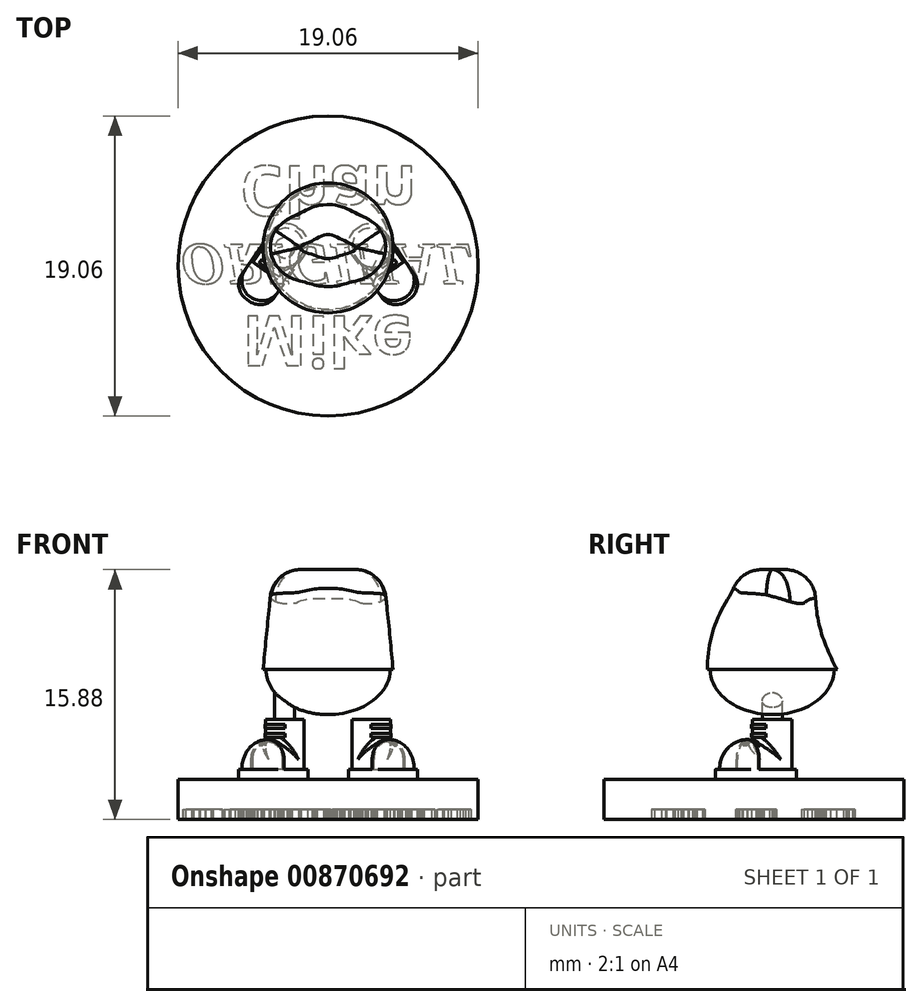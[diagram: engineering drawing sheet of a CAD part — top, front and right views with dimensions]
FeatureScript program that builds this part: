
annotation { "Feature Type Name" : "Feature", "Feature Type Description" : "" }
export const myFeature = defineFeature(function(context is Context, id is Id, definition is map)
    precondition{}
    {
        {
            var Q0;
            Q0=qCreatedBy(makeId("Top.planeOp"),FACE);
            var sketch = newSketch(context, id + "F0", { "sketchPlane" : qUnion([Q0])});
            skCircle(sketch, "E0", {"center": v(0, 0) * mm, "radius": 9.53 * mm});
            skSolve(sketch);
        }
        {
            var Q0;
            Q0=qSketchRegion(id+"F0",true);
            extrude(context, id + "F1", {"entities" : qUnion([Q0]), "depth" : 2.54 * mm, "offsetDistance" : 25.4 * mm});
        }
        {
            var Q0;
            Q0=qCreatedBy(makeId("Front.planeOp"),FACE);
            cPlane(context, id + "F2", {"entities" : qUnion([Q0]), "cplaneType" : CPlaneType.OFFSET, "offset" : 5.08 * mm, "oppositeDirection" : true, "width" : 152.4 * mm, "height" : 152.4 * mm});
        }
        {
            var Q0;
            Q0=qCreatedBy(id+"F2.planeOp",FACE);
            var sketch = newSketch(context, id + "F3", { "sketchPlane" : qUnion([Q0])});
            skLineSegment(sketch, "E1", {"start": v(0, 0) * mm, "end": v(0, 37.35) * mm, "construction": true});
            skSolve(sketch);
        }
        {
            var Q0;
            Q0=sQuery(id+"F3.wireOp",EDGE,"E1");
            var Q1;
            Q1=qCreatedBy(id+"F2.planeOp",FACE);
            cPlane(context, id + "F4", {"entities" : qUnion([Q0, Q1]), "cplaneType" : CPlaneType.LINE_ANGLE, "offset" : 25.4 * mm, "angle" : 55 * degree, "width" : 152.4 * mm, "height" : 152.4 * mm});
        }
        {
            var Q0;
            Q0=qCreatedBy(id+"F4.planeOp",FACE);
            var sketch = newSketch(context, id + "F5", { "sketchPlane" : qUnion([Q0])});
            skLineSegment(sketch, "E2", {"start": v(0, 0) * mm, "end": v(0, 19.24) * mm, "construction": true});
            skLineSegment(sketch, "E3", {"start": v(-0.89, 3.18) * mm, "end": v(4.45, 3.18) * mm});
            skArc(sketch, "E4", {"start": v(4.45, 3.18) * mm, "mid": v(3.89, 4.52) * mm, "end": v(2.54, 5.08) * mm});
            skLineSegment(sketch, "E5", {"start": v(2.54, 3.18) * mm, "end": v(2.54, 5.08) * mm});
            skLineSegment(sketch, "E6", {"start": v(2.54, 4.95) * mm, "end": v(1.9, 4.95) * mm});
            skLineSegment(sketch, "E7", {"start": v(-0.89, 3.18) * mm, "end": v(-0.89, 2.54) * mm});
            skLineSegment(sketch, "E8", {"start": v(-0.89, 2.54) * mm, "end": v(4.7, 2.54) * mm});
            skLineSegment(sketch, "E9", {"start": v(4.7, 2.54) * mm, "end": v(4.7, 3.18) * mm});
            skLineSegment(sketch, "E10", {"start": v(4.7, 3.18) * mm, "end": v(4.45, 3.18) * mm});
            skLineSegment(sketch, "E11", {"start": v(-0.64, 3.18) * mm, "end": v(-0.64, 6.35) * mm});
            skLineSegment(sketch, "E12", {"start": v(-0.64, 6.35) * mm, "end": v(1.9, 6.35) * mm});
            skLineSegment(sketch, "E13", {"start": v(1.9, 6.35) * mm, "end": v(1.9, 4.95) * mm});
            skSolve(sketch);
        }
        {
            var Q0;
            Q0=qSketchRegion(id+"F5",true);
            extrude(context, id + "F6", {"entities" : qUnion([Q0]), "endBound" : BoundingType.SYMMETRIC, "depth" : 2.54 * mm, "offsetDistance" : 25.4 * mm});
        }
        {
            var Q0;
            Q0=makeQuery(id+"F6.opExtrude","SWEPT_FACE",FACE,{"disambiguationData":[OSD([sQuery(id+"F5.wireOp",EDGE,"E5")])]});
            var sketch = newSketch(context, id + "F7", { "sketchPlane" : qUnion([Q0])});
            skLineSegment(sketch, "E14", {"start": v(4.31, 3.18) * mm, "end": v(4.06, 3.18) * mm});
            skLineSegment(sketch, "E15", {"start": v(4.06, 3.18) * mm, "end": v(4.06, 6.99) * mm});
            skLineSegment(sketch, "E16", {"start": v(4.06, 6.99) * mm, "end": v(4.31, 6.99) * mm});
            skLineSegment(sketch, "E17", {"start": v(4.31, 6.99) * mm, "end": v(4.31, 3.18) * mm});
            skLineSegment(sketch, "E18.MirrorCS", {"start": v(1.52, 6.99) * mm, "end": v(1.52, 3.18) * mm});
            skLineSegment(sketch, "E19.MirrorCS", {"start": v(1.77, 6.99) * mm, "end": v(1.52, 6.99) * mm});
            skLineSegment(sketch, "E20.MirrorCS", {"start": v(1.77, 3.18) * mm, "end": v(1.77, 6.99) * mm});
            skPoint(sketch, "E21.orphan", {"position": v(1.23, 3.18) * mm});
            skLineSegment(sketch, "E22.trimOffspring", {"start": v(1.77, 3.18) * mm, "end": v(1.52, 3.18) * mm});
            skSolve(sketch);
        }
        {
            var Q0;
            Q0=qSketchRegion(id+"F7",true);
            extrude(context, id + "F8", {"entities" : qUnion([Q0]), "operationType" : NewBodyOperationType.REMOVE, "endBound" : BoundingType.THROUGH_ALL, "depth" : 25.4 * mm, "offsetDistance" : 25.4 * mm});
        }
        {
            var Q0;
            Q0=makeQuery(id+"F8.boolean.opBoolean","INTERSECT",EDGE,{"derivedFrom":[makeQuery(id+"F6.opExtrude","SWEPT_FACE",FACE,{"disambiguationData":[OSD([sQuery(id+"F5.wireOp",EDGE,"E6")])]}),makeQuery(id+"F8.opExtrude","SWEPT_FACE",FACE,{"disambiguationData":[OSD([sQuery(id+"F7.wireOp",EDGE,"E15")])]})]});
            var Q1;
            Q1=makeQuery(id+"F8.boolean.opBoolean","INTERSECT",EDGE,{"derivedFrom":[makeQuery(id+"F6.opExtrude","SWEPT_FACE",FACE,{"disambiguationData":[OSD([sQuery(id+"F5.wireOp",EDGE,"E6")])]}),makeQuery(id+"F8.opExtrude","SWEPT_FACE",FACE,{"disambiguationData":[OSD([sQuery(id+"F7.wireOp",EDGE,"E20.MirrorCS")])]})]});
            var Q2;
            Q2=makeQuery(id+"F8.boolean.opBoolean","INTERSECT",EDGE,{"derivedFrom":[makeQuery(id+"F6.opExtrude","SWEPT_FACE",FACE,{"disambiguationData":[OSD([sQuery(id+"F5.wireOp",EDGE,"E13")])]}),makeQuery(id+"F8.opExtrude","SWEPT_FACE",FACE,{"disambiguationData":[OSD([sQuery(id+"F7.wireOp",EDGE,"E15")])]})]});
            var Q3;
            Q3=makeQuery(id+"F8.boolean.opBoolean","INTERSECT",EDGE,{"derivedFrom":[makeQuery(id+"F6.opExtrude","SWEPT_FACE",FACE,{"disambiguationData":[OSD([sQuery(id+"F5.wireOp",EDGE,"E13")])]}),makeQuery(id+"F8.opExtrude","SWEPT_FACE",FACE,{"disambiguationData":[OSD([sQuery(id+"F7.wireOp",EDGE,"E20.MirrorCS")])]})]});
            var Q4;
            Q4=makeQuery(id+"F8.boolean.opBoolean","INTERSECT",EDGE,{"derivedFrom":[makeQuery(id+"F6.opExtrude","SWEPT_FACE",FACE,{"disambiguationData":[OSD([sQuery(id+"F5.wireOp",EDGE,"E11")])]}),makeQuery(id+"F8.opExtrude","SWEPT_FACE",FACE,{"disambiguationData":[OSD([sQuery(id+"F7.wireOp",EDGE,"E20.MirrorCS")])]})]});
            var Q5;
            Q5=makeQuery(id+"F8.boolean.opBoolean","INTERSECT",EDGE,{"derivedFrom":[makeQuery(id+"F6.opExtrude","SWEPT_FACE",FACE,{"disambiguationData":[OSD([sQuery(id+"F5.wireOp",EDGE,"E11")])]}),makeQuery(id+"F8.opExtrude","SWEPT_FACE",FACE,{"disambiguationData":[OSD([sQuery(id+"F7.wireOp",EDGE,"E15")])]})]});
            fillet(context, id + "F9", {"entities" : qUnion([Q0, Q1, Q2, Q3, Q4, Q5]), "radius" : 1.14 * mm, "tangentPropagation" : true, "allowEdgeOverflow" : false});
        }
        {
            var Q0;
            Q0=makeQuery(id+"F6.opExtrude","CAP_EDGE",EDGE,{"disambiguationData":[OSD([sQuery(id+"F5.wireOp",EDGE,"E4")])],"isStart":false});
            var Q1;
            Q1=makeQuery(id+"F6.opExtrude","CAP_EDGE",EDGE,{"disambiguationData":[OSD([sQuery(id+"F5.wireOp",EDGE,"E4")])],"isStart":true});
            fillet(context, id + "F10", {"entities" : qUnion([Q0, Q1]), "radius" : 1.27 * mm, "tangentPropagation" : true, "allowEdgeOverflow" : false});
        }
        {
            var Q0;
            Q0=makeQuery(id+"F6.opExtrude","CAP_EDGE",EDGE,{"disambiguationData":[OSD([sQuery(id+"F5.wireOp",EDGE,"E9")])],"isStart":false});
            var Q1;
            Q1=makeQuery(id+"F6.opExtrude","CAP_EDGE",EDGE,{"disambiguationData":[OSD([sQuery(id+"F5.wireOp",EDGE,"E7")])],"isStart":false});
            var Q2;
            Q2=makeQuery(id+"F6.opExtrude","CAP_EDGE",EDGE,{"disambiguationData":[OSD([sQuery(id+"F5.wireOp",EDGE,"E7")])],"isStart":true});
            var Q3;
            Q3=makeQuery(id+"F6.opExtrude","CAP_EDGE",EDGE,{"disambiguationData":[OSD([sQuery(id+"F5.wireOp",EDGE,"E9")])],"isStart":true});
            fillet(context, id + "F11", {"entities" : qUnion([Q0, Q1, Q2, Q3]), "radius" : 1.14 * mm, "tangentPropagation" : true, "allowEdgeOverflow" : false});
        }
        {
            var Q0;
            {var subQ0=makeQuery(id+"F8.opExtrude","SWEPT_FACE",FACE,{"disambiguationData":[OSD([sQuery(id+"F7.wireOp",EDGE,"E15")])]});Q0=makeQuery(id+"F9.opFillet","BLEND_EDGE",EDGE,{"blendedFrom":[makeQuery(id+"F8.boolean.opBoolean","INTERSECT",EDGE,{"derivedFrom":[makeQuery(id+"F6.opExtrude","SWEPT_FACE",FACE,{"disambiguationData":[OSD([sQuery(id+"F5.wireOp",EDGE,"E6")])]}),subQ0]}),makeQuery(id+"F8.boolean.opBoolean","INTERSECT",EDGE,{"derivedFrom":[makeQuery(id+"F6.opExtrude","SWEPT_FACE",FACE,{"disambiguationData":[OSD([sQuery(id+"F5.wireOp",EDGE,"E13")])]}),subQ0]})],"blendedInto":[]});}
            fillet(context, id + "F12", {"entities" : qUnion([Q0]), "radius" : 0.38 * mm, "tangentPropagation" : true, "allowEdgeOverflow" : false});
        }
        {
            var Q0;
            Q0=qCreatedBy(id+"F4.planeOp",FACE);
            var sketch = newSketch(context, id + "F13", { "sketchPlane" : qUnion([Q0])});
            skLineSegment(sketch, "E23", {"start": v(2.1, 4.76) * mm, "end": v(2.1, 5.02) * mm});
            skLineSegment(sketch, "E24", {"start": v(2.1, 5.02) * mm, "end": v(2.35, 5.02) * mm});
            skLineSegment(sketch, "E25", {"start": v(2.35, 5.02) * mm, "end": v(2.35, 4.76) * mm});
            skLineSegment(sketch, "E26", {"start": v(2.35, 4.76) * mm, "end": v(2.35, 4.76) * mm});
            skLineSegment(sketch, "E27", {"start": v(2.35, 4.76) * mm, "end": v(2.1, 4.76) * mm});
            skLineSegment(sketch, "E28", {"start": v(0.18, 3.8) * mm, "end": v(2.97, 3.81) * mm, "construction": true});
            skSolve(sketch);
        }
        {
            var Q0;
            Q0=makeQuery(id+"F13.imprint","IMPRINT",FACE,{"disambiguationData":[TD([[makeQuery(id+"F13.imprint","IMPRINT",EDGE,{"derivedFrom":sQuery(id+"F13.wireOp",EDGE,"E23")}),-1.0]])]});
            var Q1;
            Q1=sQuery(id+"F13.wireOp",EDGE,"E28");
            revolve(context, id + "F14", {"operationType" : NewBodyOperationType.ADD, "surfaceOperationType" : NewSurfaceOperationType.NEW, "entities" : qUnion([Q0]), "axis" : qUnion([Q1]), "revolveType" : RevolveType.SYMMETRIC, "angle" : 80 * degree});
        }
        {
            var Q0;
            Q0=qCreatedBy(id+"F4.planeOp",FACE);
            var sketch = newSketch(context, id + "F15", { "sketchPlane" : qUnion([Q0])});
            skLineSegment(sketch, "E29", {"start": v(1.97, 6.03) * mm, "end": v(1.97, 5.78) * mm});
            skLineSegment(sketch, "E30", {"start": v(1.97, 5.46) * mm, "end": v(1.04, 5.46) * mm});
            skLineSegment(sketch, "E31", {"start": v(1.04, 5.46) * mm, "end": v(1.04, 5.2) * mm});
            skLineSegment(sketch, "E32", {"start": v(1.04, 5.2) * mm, "end": v(1.97, 5.2) * mm});
            skLineSegment(sketch, "E33", {"start": v(1.97, 5.78) * mm, "end": v(1.05, 5.78) * mm});
            skLineSegment(sketch, "E34", {"start": v(1.05, 5.78) * mm, "end": v(1.05, 6.03) * mm});
            skLineSegment(sketch, "E35", {"start": v(1.05, 6.03) * mm, "end": v(1.97, 6.03) * mm});
            skLineSegment(sketch, "E36.trimOffspring", {"start": v(1.97, 5.46) * mm, "end": v(1.97, 5.2) * mm});
            skLineSegment(sketch, "E37", {"start": v(0.76, 6.83) * mm, "end": v(0.76, 4.3) * mm, "construction": true});
            skSolve(sketch);
        }
        {
            var Q0;
            Q0=qSketchRegion(id+"F15",true);
            var Q1;
            Q1=sQuery(id+"F15.wireOp",EDGE,"E37");
            revolve(context, id + "F16", {"operationType" : NewBodyOperationType.ADD, "surfaceOperationType" : NewSurfaceOperationType.NEW, "entities" : qUnion([Q0]), "axis" : qUnion([Q1]), "revolveType" : RevolveType.SYMMETRIC, "angle" : 80 * degree});
        }
        {
            var Q0;
            Q0=makeQuery(id+"F6.opExtrude","SWEPT_BODY",BODY,{"disambiguationData":[OSD([sQuery(id+"F5.wireOp",EDGE,"E3"),sQuery(id+"F5.wireOp",EDGE,"E4"),sQuery(id+"F5.wireOp",EDGE,"E5"),sQuery(id+"F5.wireOp",EDGE,"E6"),sQuery(id+"F5.wireOp",EDGE,"E7"),sQuery(id+"F5.wireOp",EDGE,"E8"),sQuery(id+"F5.wireOp",EDGE,"E9"),sQuery(id+"F5.wireOp",EDGE,"E10"),sQuery(id+"F5.wireOp",EDGE,"E11"),sQuery(id+"F5.wireOp",EDGE,"E12"),sQuery(id+"F5.wireOp",EDGE,"E13")])]});
            var Q1;
            Q1=qCreatedBy(makeId("Right.planeOp"),FACE);
            mirror(context, id + "F17", {"operationType" : NewBodyOperationType.ADD, "entities" : qUnion([Q0]), "mirrorPlane" : qUnion([Q1])});
        }
        {
            var Q0;
            Q0=qCreatedBy(id+"F4.planeOp",FACE);
            var sketch = newSketch(context, id + "F18", { "sketchPlane" : qUnion([Q0])});
            skLineSegment(sketch, "E38", {"start": v(0.64, 6.35) * mm, "end": v(0.64, 1.2) * mm, "construction": true});
            skSolve(sketch);
        }
        {
            var Q0;
            Q0=sQuery(id+"F18.wireOp",VERTEX,"E38.start");
            var Q1;
            Q1=qCreatedBy(makeId("Front.planeOp"),FACE);
            cPlane(context, id + "F19", {"entities" : qUnion([Q0, Q1]), "cplaneType" : CPlaneType.PLANE_POINT, "offset" : 25.4 * mm, "width" : 152.4 * mm, "height" : 152.4 * mm});
        }
        {
            var Q0;
            Q0=qCreatedBy(id+"F19.planeOp",FACE);
            var sketch = newSketch(context, id + "F20", { "sketchPlane" : qUnion([Q0])});
            skLineSegment(sketch, "E39", {"start": v(-2.75, 6.1) * mm, "end": v(-2.75, 14.9) * mm, "construction": true});
            skLineSegment(sketch, "E40", {"start": v(-2.75, 6.35) * mm, "end": v(-3.39, 6.35) * mm});
            skLineSegment(sketch, "E41", {"start": v(-3.39, 6.35) * mm, "end": v(-3.39, 8.26) * mm});
            skLineSegment(sketch, "E42", {"start": v(-3.39, 8.26) * mm, "end": v(-2.75, 8.26) * mm});
            skLineSegment(sketch, "E43", {"start": v(-2.75, 8.26) * mm, "end": v(-2.75, 6.35) * mm});
            skSolve(sketch);
        }
        {
            var Q0;
            Q0=qSketchRegion(id+"F20",true);
            var Q1;
            Q1=sQuery(id+"F20.wireOp",EDGE,"E43");
            revolve(context, id + "F21", {"operationType" : NewBodyOperationType.ADD, "surfaceOperationType" : NewSurfaceOperationType.NEW, "entities" : qUnion([Q0]), "axis" : qUnion([Q1]), "revolveType" : RevolveType.FULL});
        }
        {
            var Q0;
            Q0=qCreatedBy(id+"F19.planeOp",FACE);
            var sketch = newSketch(context, id + "F22", { "sketchPlane" : qUnion([Q0])});
            skLineSegment(sketch, "E44", {"start": v(-3.94, 9.52) * mm, "end": v(0, 9.52) * mm});
            skLineSegment(sketch, "E45", {"start": v(0, 9.52) * mm, "end": v(0, 6.67) * mm});
            skEllipticalArc(sketch, "E46", {});
            const initialGuessF22  = {"E46": [0, 0.009525, -1, 0, 0.003937, 0.0028575000000000002, 0, 1.5707963267948966]};
            skSetInitialGuess(sketch, initialGuessF22);
            skSolve(sketch);
        }
        {
            var Q0;
            Q0=qSketchRegion(id+"F22",true);
            var Q1;
            Q1=sQuery(id+"F22.wireOp",EDGE,"E45");
            revolve(context, id + "F23", {"operationType" : NewBodyOperationType.ADD, "surfaceOperationType" : NewSurfaceOperationType.NEW, "entities" : qUnion([Q0]), "axis" : qUnion([Q1]), "revolveType" : RevolveType.FULL});
        }
        {
            var Q0;
            Q0=makeQuery(id+"F23.opRevolve","SWEPT_FACE",FACE,{"disambiguationData":[OSD([sQuery(id+"F22.wireOp",EDGE,"E44")])]});
            cPlane(context, id + "F24", {"entities" : qUnion([Q0]), "cplaneType" : CPlaneType.OFFSET, "offset" : 6.35 * mm, "width" : 152.4 * mm, "height" : 152.4 * mm});
        }
        {
            var Q0;
            Q0=qCreatedBy(id+"F24.planeOp",FACE);
            var sketch = newSketch(context, id + "F25", { "sketchPlane" : qUnion([Q0])});
            skLineSegment(sketch, "E47", {"start": v(-7.35, 1.15) * mm, "end": v(6.96, 1.15) * mm, "construction": true});
            skCircle(sketch, "E48", {"center": v(0, 1.15) * mm, "radius": 3.94 * mm, "construction": true});
            skArc(sketch, "E49", {"start": v(-1.27, 3.37) * mm, "mid": v(-3.5, 1.15) * mm, "end": v(-1.27, -1.07) * mm});
            skLineSegment(sketch, "E50", {"start": v(0, 1.15) * mm, "end": v(0, 9.01) * mm, "construction": true});
            skLineSegment(sketch, "E51", {"start": v(-1.27, 3.37) * mm, "end": v(0, 3.37) * mm});
            skArc(sketch, "E52.MirrorCS", {"start": v(1.27, 3.37) * mm, "mid": v(3.5, 1.15) * mm, "end": v(1.27, -1.07) * mm});
            skLineSegment(sketch, "E53.MirrorCS", {"start": v(1.27, 3.37) * mm, "end": v(0, 3.37) * mm});
            skLineSegment(sketch, "E54.MirrorCS", {"start": v(1.27, -1.07) * mm, "end": v(0, -1.07) * mm});
            skLineSegment(sketch, "E55.MirrorCS", {"start": v(-1.27, -1.07) * mm, "end": v(0, -1.07) * mm});
            skPoint(sketch, "E56.orphan", {"position": v(0, 2.98) * mm});
            skSolve(sketch);
        }
        {
            var Q0;
            Q0=makeQuery(id+"F23.opRevolve","SWEPT_FACE",FACE,{"disambiguationData":[OSD([sQuery(id+"F22.wireOp",EDGE,"E44")])]});
            var sketch = newSketch(context, id + "F26", { "sketchPlane" : qUnion([Q0])});
            skCircle(sketch, "E57", {"center": v(0, 1.15) * mm, "radius": 4.13 * mm});
            skSolve(sketch);
        }
        {
            var Q0;
            Q0=qCreatedBy(makeId("Right.planeOp"),FACE);
            var sketch = newSketch(context, id + "F27", { "sketchPlane" : qUnion([Q0])});
            skLineSegment(sketch, "E58", {"start": v(-9.7, 15.88) * mm, "end": v(-1.07, 15.88) * mm, "construction": true});
            skPoint(sketch, "E59", {"position": v(-5.39, 15.88) * mm});
            skLineSegment(sketch, "E60", {"start": v(7.04, 9.52) * mm, "end": v(-2.98, 9.52) * mm, "construction": true});
            skArc(sketch, "E61", {"start": v(-1.6, 14.13) * mm, "mid": v(-2.62, 11.93) * mm, "end": v(-2.98, 9.53) * mm});
            skArc(sketch, "E62", {"start": v(-1.6, 14.13) * mm, "mid": v(-1.2, 14.96) * mm, "end": v(-1.07, 15.88) * mm});
            skSolve(sketch);
        }
        {
            var Q0;
            Q0=qBodyType(qCreatedBy(id+"F27",EDGE),BodyType.WIRE);
            var Q2;
            Q2=qSketchRegion(id+"F26",true);
            var Q3;
            Q3=qSketchRegion(id+"F25",true);
            var Q4;
            Q4=qBodyType(qCreatedBy(id+"F27",EDGE),BodyType.WIRE);
            loft(context, id + "F28", {"operationType" : NewBodyOperationType.ADD, "spine" : qUnion([Q0]), "addGuides" : true, "sheetProfilesArray" : [{ "sheetProfileEntities" : qUnion([Q2]) }, { "sheetProfileEntities" : qUnion([Q3]) }], "guidesArray" : [{ "guideEntities" : qUnion([Q4]), "guideDerivativeType" : LoftGuideDerivativeType.DEFAULT, "guideDerivativeMagnitude" : 1 }]});
        }
        {
            var Q0;
            Q0=makeQuery(id+"F28.opLoft","MID_CAP_EDGE",EDGE,{"disambiguationData":[OSD([sQuery(id+"F25.wireOp",EDGE,"E49"),sQuery(id+"F25.wireOp",EDGE,"E55.MirrorCS"),sQuery(id+"F27.wireOp",EDGE,"E62")])],"capPos":1.0});
            fillet(context, id + "F29", {"entities" : qUnion([Q0]), "radius" : 1.9 * mm, "tangentPropagation" : true, "allowEdgeOverflow" : false});
        }
        {
            var Q0;
            Q0=makeQuery(id+"F1.opExtrude","CAP_FACE",FACE,{"disambiguationData":[OSD([sQuery(id+"F0.wireOp",EDGE,"E0")])],"isStart":true});
            var sketch = newSketch(context, id + "F30", { "sketchPlane" : qUnion([Q0])});
            skText(sketch, "E63", { "text": "Mike", "fontName": "OpenSans-Bold.ttf"});
            skText(sketch, "E64", { "text": "Chan", "fontName": "OpenSans-Bold.ttf"});
            skText(sketch, "E65", { "text": "ORIGINAL", "fontName": "Tinos-BoldItalic.ttf"});
            skLineSegment(sketch, "E66", {"start": v(0, 9.53) * mm, "end": v(0, -9.53) * mm, "construction": true});
            const initialGuessF30  = {"E63": [-0.00547, 0.00317, 1, 0, 0.00318], "E64": [-0.00561, -0.00635, 1, 0, 0.00317], "E65": [-0.00935, -0.00137, 1, 0, 0.00274]};
            skSetInitialGuess(sketch, initialGuessF30);
            skSolve(sketch);
        }
        {
            var Q0;
            Q0=qSketchRegion(id+"F30",true);
            extrude(context, id + "F31", {"entities" : qUnion([Q0]), "operationType" : NewBodyOperationType.REMOVE, "oppositeDirection" : true, "depth" : 0.64 * mm, "offsetDistance" : 25.4 * mm});
        }
    });
